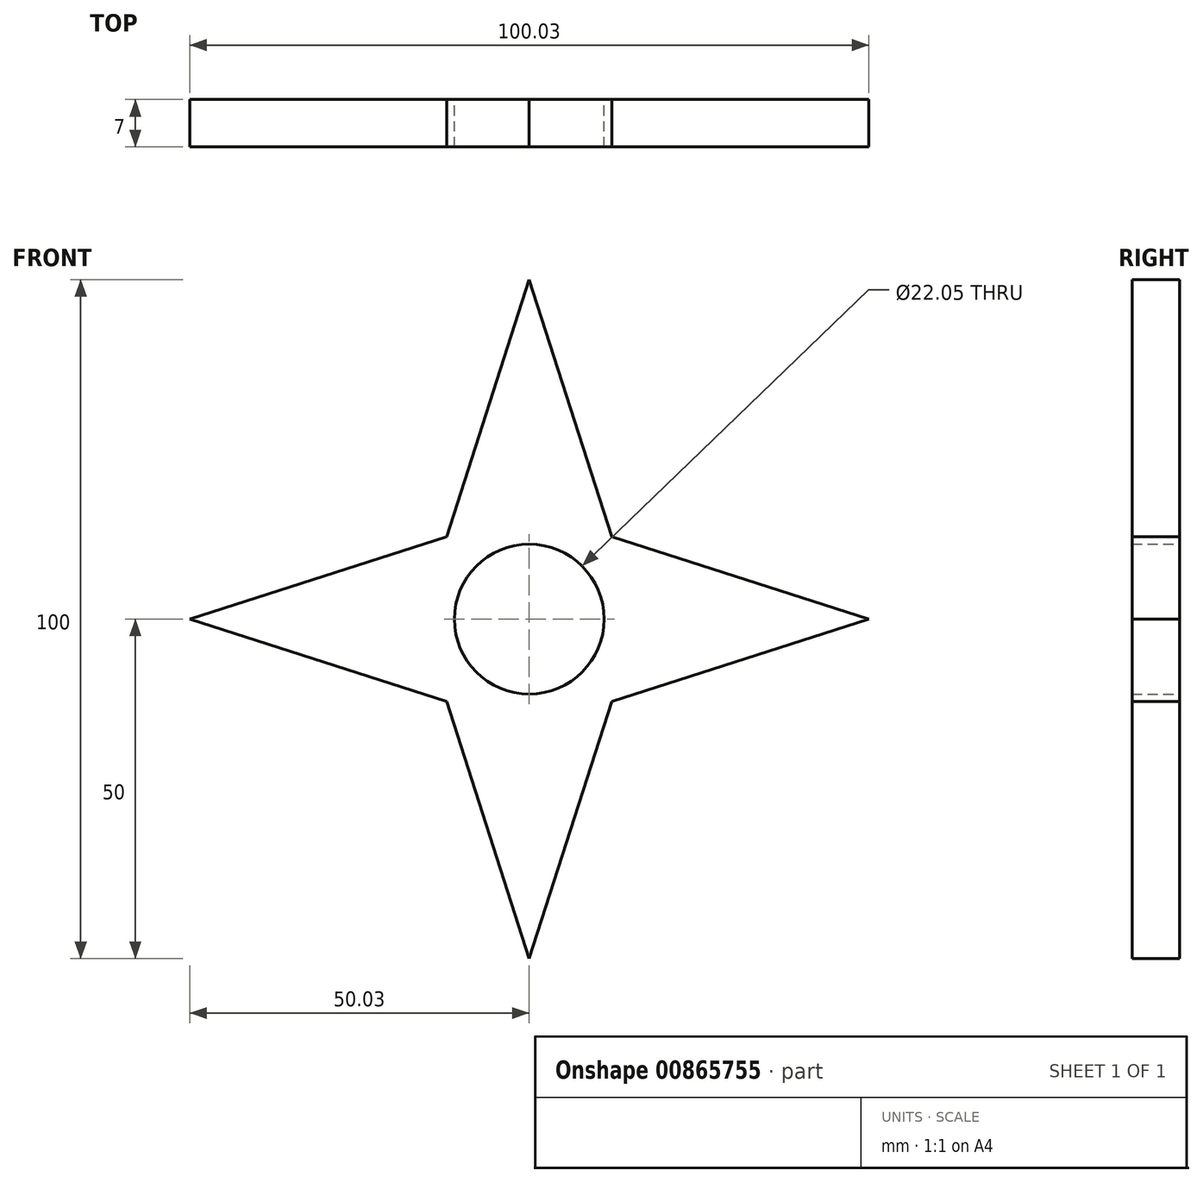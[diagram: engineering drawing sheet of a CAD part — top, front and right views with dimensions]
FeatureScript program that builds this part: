
annotation { "Feature Type Name" : "Feature", "Feature Type Description" : "" }
export const myFeature = defineFeature(function(context is Context, id is Id, definition is map)
    precondition{}
    {
        {
            var Q0;
            Q0=qCreatedBy(makeId("Front.planeOp"),FACE);
            var sketch = newSketch(context, id + "F0", { "sketchPlane" : qUnion([Q0])});
            skCircle(sketch, "E0", {"center": v(0, 0) * mm, "radius": 16.02 * mm});
            skCircle(sketch, "E1", {"center": v(0, 0) * mm, "radius": 11.03 * mm});
            skLineSegment(sketch, "E2", {"start": v(-16.02, 0) * mm, "end": v(0, 50) * mm});
            skLineSegment(sketch, "E3", {"start": v(0, 50) * mm, "end": v(16.02, 0) * mm});
            skLineSegment(sketch, "E4", {"start": v(0, -50) * mm, "end": v(-16.03, 0) * mm});
            skLineSegment(sketch, "E5", {"start": v(0, -50) * mm, "end": v(16.02, 0) * mm});
            skLineSegment(sketch, "E6", {"start": v(0, 0) * mm, "end": v(16.02, 0) * mm});
            skLineSegment(sketch, "E7", {"start": v(0, 0) * mm, "end": v(0, -16.02) * mm});
            skLineSegment(sketch, "E8", {"start": v(0, -16.02) * mm, "end": v(-50.03, 0) * mm});
            skLineSegment(sketch, "E9", {"start": v(0, 0) * mm, "end": v(0, 16.02) * mm});
            skLineSegment(sketch, "E10", {"start": v(0, 16.02) * mm, "end": v(-50.03, 0) * mm});
            skLineSegment(sketch, "E11", {"start": v(0, 16.02) * mm, "end": v(50, 0) * mm});
            skLineSegment(sketch, "E12", {"start": v(50, 0) * mm, "end": v(0, -16.02) * mm});
            skSolve(sketch);
        }
        {
            var Q0;
            {var subQ5=sQuery(id+"F0.wireOp",EDGE,"E10");var subQ7=sQuery(id+"F0.wireOp",EDGE,"E2");var subQ8=makeQuery(id+"F0.imprint","INTERSECT",VERTEX,{"derivedFrom":[subQ7,subQ5]});Q0=makeQuery(id+"F0.imprint","IMPRINT",FACE,{"disambiguationData":[TD([[makeQuery(id+"F0.imprint","IMPRINT",EDGE,{"disambiguationData":[TD([[subQ8,1.0]])],"derivedFrom":subQ7}),1.0]])]});}
            var Q1;
            {var subQ0=sQuery(id+"F0.wireOp",EDGE,"E5");var subQ1=sQuery(id+"F0.wireOp",EDGE,"E4");var subQ2=makeQuery(id+"F0.imprint","INTERSECT",VERTEX,{"derivedFrom":[subQ1,subQ0]});Q1=makeQuery(id+"F0.imprint","IMPRINT",FACE,{"disambiguationData":[TD([[makeQuery(id+"F0.imprint","IMPRINT",EDGE,{"disambiguationData":[TD([[subQ2,-1.0]])],"derivedFrom":subQ1}),-1.0]])]});}
            var Q2;
            {var subQ0=sQuery(id+"F0.wireOp",EDGE,"E12");var subQ1=sQuery(id+"F0.wireOp",EDGE,"E0");var subQ2=makeQuery(id+"F0.imprint","INTERSECT",VERTEX,{"derivedFrom":[subQ1,subQ0]});Q2=makeQuery(id+"F0.imprint","IMPRINT",FACE,{"disambiguationData":[TD([[makeQuery(id+"F0.imprint","IMPRINT",EDGE,{"disambiguationData":[TD([[subQ2,-1.0]])],"derivedFrom":subQ1}),-1.0]])]});}
            var Q3;
            {var subQ0=sQuery(id+"F0.wireOp",EDGE,"E12");var subQ1=sQuery(id+"F0.wireOp",EDGE,"E0");var subQ3=makeQuery(id+"F0.imprint","INTERSECT",VERTEX,{"derivedFrom":[subQ1,subQ0]});Q3=makeQuery(id+"F0.imprint","IMPRINT",FACE,{"disambiguationData":[TD([[makeQuery(id+"F0.imprint","IMPRINT",EDGE,{"disambiguationData":[TD([[subQ3,1.0]])],"derivedFrom":subQ1}),1.0]])]});}
            var Q4;
            {var subQ0=sQuery(id+"F0.wireOp",EDGE,"E8");var subQ1=sQuery(id+"F0.wireOp",EDGE,"E0");var subQ3=makeQuery(id+"F0.imprint","INTERSECT",VERTEX,{"derivedFrom":[subQ1,subQ0]});Q4=makeQuery(id+"F0.imprint","IMPRINT",FACE,{"disambiguationData":[TD([[makeQuery(id+"F0.imprint","IMPRINT",EDGE,{"disambiguationData":[TD([[subQ3,-1.0]])],"derivedFrom":subQ1}),1.0]])]});}
            var Q5;
            {var subQ0=sQuery(id+"F0.wireOp",EDGE,"E4");var subQ1=sQuery(id+"F0.wireOp",EDGE,"E0");var subQ2=makeQuery(id+"F0.imprint","INTERSECT",VERTEX,{"derivedFrom":[subQ1,subQ0]});Q5=makeQuery(id+"F0.imprint","IMPRINT",FACE,{"disambiguationData":[TD([[makeQuery(id+"F0.imprint","IMPRINT",EDGE,{"disambiguationData":[TD([[subQ2,-1.0]])],"derivedFrom":subQ1}),-1.0]])]});}
            var Q6;
            {var subQ0=sQuery(id+"F0.wireOp",EDGE,"E4");var subQ1=sQuery(id+"F0.wireOp",EDGE,"E0");var subQ3=makeQuery(id+"F0.imprint","INTERSECT",VERTEX,{"derivedFrom":[subQ1,subQ0]});Q6=makeQuery(id+"F0.imprint","IMPRINT",FACE,{"disambiguationData":[TD([[makeQuery(id+"F0.imprint","IMPRINT",EDGE,{"disambiguationData":[TD([[subQ3,1.0]])],"derivedFrom":subQ1}),1.0]])]});}
            var Q7;
            {var subQ0=sQuery(id+"F0.wireOp",EDGE,"E2");var subQ1=sQuery(id+"F0.wireOp",EDGE,"E0");var subQ3=makeQuery(id+"F0.imprint","INTERSECT",VERTEX,{"derivedFrom":[subQ1,subQ0]});Q7=makeQuery(id+"F0.imprint","IMPRINT",FACE,{"disambiguationData":[TD([[makeQuery(id+"F0.imprint","IMPRINT",EDGE,{"disambiguationData":[TD([[subQ3,-1.0]])],"derivedFrom":subQ1}),1.0]])]});}
            var Q8;
            {var subQ0=sQuery(id+"F0.wireOp",EDGE,"E10");var subQ1=sQuery(id+"F0.wireOp",EDGE,"E0");var subQ2=makeQuery(id+"F0.imprint","INTERSECT",VERTEX,{"derivedFrom":[subQ1,subQ0]});Q8=makeQuery(id+"F0.imprint","IMPRINT",FACE,{"disambiguationData":[TD([[makeQuery(id+"F0.imprint","IMPRINT",EDGE,{"disambiguationData":[TD([[subQ2,-1.0]])],"derivedFrom":subQ1}),-1.0]])]});}
            var Q9;
            {var subQ0=sQuery(id+"F0.wireOp",EDGE,"E11");var subQ1=sQuery(id+"F0.wireOp",EDGE,"E0");var subQ3=makeQuery(id+"F0.imprint","INTERSECT",VERTEX,{"derivedFrom":[subQ1,subQ0]});Q9=makeQuery(id+"F0.imprint","IMPRINT",FACE,{"disambiguationData":[TD([[makeQuery(id+"F0.imprint","IMPRINT",EDGE,{"disambiguationData":[TD([[subQ3,-1.0]])],"derivedFrom":subQ1}),1.0]])]});}
            var Q10;
            {var subQ0=sQuery(id+"F0.wireOp",EDGE,"E10");var subQ1=sQuery(id+"F0.wireOp",EDGE,"E0");var subQ3=makeQuery(id+"F0.imprint","INTERSECT",VERTEX,{"derivedFrom":[subQ1,subQ0]});Q10=makeQuery(id+"F0.imprint","IMPRINT",FACE,{"disambiguationData":[TD([[makeQuery(id+"F0.imprint","IMPRINT",EDGE,{"disambiguationData":[TD([[subQ3,1.0]])],"derivedFrom":subQ1}),1.0]])]});}
            var Q11;
            {var subQ0=sQuery(id+"F0.wireOp",EDGE,"E3");var subQ1=sQuery(id+"F0.wireOp",EDGE,"E2");var subQ2=makeQuery(id+"F0.imprint","INTERSECT",VERTEX,{"derivedFrom":[subQ1,subQ0]});Q11=makeQuery(id+"F0.imprint","IMPRINT",FACE,{"disambiguationData":[TD([[makeQuery(id+"F0.imprint","IMPRINT",EDGE,{"disambiguationData":[TD([[subQ2,1.0]])],"derivedFrom":subQ1}),-1.0]])]});}
            var Q12;
            {var subQ0=sQuery(id+"F0.wireOp",EDGE,"E3");var subQ1=sQuery(id+"F0.wireOp",EDGE,"E0");var subQ2=makeQuery(id+"F0.imprint","INTERSECT",VERTEX,{"derivedFrom":[subQ1,subQ0]});Q12=makeQuery(id+"F0.imprint","IMPRINT",FACE,{"disambiguationData":[TD([[makeQuery(id+"F0.imprint","IMPRINT",EDGE,{"disambiguationData":[TD([[subQ2,-1.0]])],"derivedFrom":subQ1}),-1.0]])]});}
            var Q13;
            {var subQ0=sQuery(id+"F0.wireOp",EDGE,"E3");var subQ1=sQuery(id+"F0.wireOp",EDGE,"E0");var subQ3=makeQuery(id+"F0.imprint","INTERSECT",VERTEX,{"derivedFrom":[subQ1,subQ0]});Q13=makeQuery(id+"F0.imprint","IMPRINT",FACE,{"disambiguationData":[TD([[makeQuery(id+"F0.imprint","IMPRINT",EDGE,{"disambiguationData":[TD([[subQ3,1.0]])],"derivedFrom":subQ1}),1.0]])]});}
            var Q14;
            {var subQ0=sQuery(id+"F0.wireOp",EDGE,"E5");var subQ1=sQuery(id+"F0.wireOp",EDGE,"E0");var subQ3=makeQuery(id+"F0.imprint","INTERSECT",VERTEX,{"derivedFrom":[subQ1,subQ0]});Q14=makeQuery(id+"F0.imprint","IMPRINT",FACE,{"disambiguationData":[TD([[makeQuery(id+"F0.imprint","IMPRINT",EDGE,{"disambiguationData":[TD([[subQ3,-1.0]])],"derivedFrom":subQ1}),1.0]])]});}
            var Q15;
            {var subQ0=sQuery(id+"F0.wireOp",EDGE,"E11");var subQ1=sQuery(id+"F0.wireOp",EDGE,"E3");var subQ2=makeQuery(id+"F0.imprint","INTERSECT",VERTEX,{"derivedFrom":[subQ1,subQ0]});Q15=makeQuery(id+"F0.imprint","IMPRINT",FACE,{"disambiguationData":[TD([[makeQuery(id+"F0.imprint","IMPRINT",EDGE,{"disambiguationData":[TD([[subQ2,-1.0]])],"derivedFrom":subQ1}),1.0]])]});}
            var Q16;
            {var subQ2=sQuery(id+"F0.wireOp",EDGE,"E0");var subQ9=sQuery(id+"F0.wireOp",EDGE,"E12");var subQ10=makeQuery(id+"F0.imprint","INTERSECT",VERTEX,{"derivedFrom":[subQ2,subQ9]});Q16=makeQuery(id+"F0.imprint","IMPRINT",FACE,{"disambiguationData":[TD([[makeQuery(id+"F0.imprint","IMPRINT",EDGE,{"disambiguationData":[TD([[subQ10,-1.0]])],"derivedFrom":subQ2}),1.0]])]});}
            var Q17;
            {var subQ2=sQuery(id+"F0.wireOp",EDGE,"E0");var subQ5=sQuery(id+"F0.wireOp",EDGE,"E10");var subQ6=makeQuery(id+"F0.imprint","INTERSECT",VERTEX,{"derivedFrom":[subQ2,subQ5]});Q17=makeQuery(id+"F0.imprint","IMPRINT",FACE,{"disambiguationData":[TD([[makeQuery(id+"F0.imprint","IMPRINT",EDGE,{"disambiguationData":[TD([[subQ6,-1.0]])],"derivedFrom":subQ2}),1.0]])]});}
            var Q18;
            {var subQ1=sQuery(id+"F0.wireOp",EDGE,"E3");var subQ2=sQuery(id+"F0.wireOp",EDGE,"E0");var subQ10=makeQuery(id+"F0.imprint","INTERSECT",VERTEX,{"derivedFrom":[subQ2,subQ1]});Q18=makeQuery(id+"F0.imprint","IMPRINT",FACE,{"disambiguationData":[TD([[makeQuery(id+"F0.imprint","IMPRINT",EDGE,{"disambiguationData":[TD([[subQ10,-1.0]])],"derivedFrom":subQ2}),1.0]])]});}
            extrude(context, id + "F1", {"entities" : qUnion([Q0, Q1, Q2, Q3, Q4, Q5, Q6, Q7, Q8, Q9, Q10, Q11, Q12, Q13, Q14, Q15, Q16, Q17, Q18]), "depth" : 7 * mm, "offsetDistance" : 25 * mm});
        }
    });
